FCSTD DOCUMENT  (FreeCAD 1.0R39319 (Git))
Label: KNOB-TEK2_assembly_tool_assy
License: All rights reserved
LicenseURL: https://en.wikipedia.org/wiki/All_rights_reserved
objects: App::DocumentObjectGroup×3, App::Link×3, PartDesign::CoordinateSystem×1, App::FeaturePython×1, App::Part×1
note: 1 computed .brp shape members not serialized (recipe doc carries the construction recipe); baked Part::Feature solids carry a one-line shape summary decoded from their .brp
EXTERNAL_REF file=../../Mechanical/Design/KNOB-TEK2/KNOB-TEK2.FCStd obj=LCS_1
EXTERNAL_REF file=../../Mechanical/Design/KNOB-TEK2/KNOB-TEK2.FCStd obj=Body
EXTERNAL_REF file=../../Mechanical/Design/KNOB-TEK2/KNOB-TEK2.FCStd obj=LCS_2
EXTERNAL_REF file=../../Mechanical/Design/PLASTIC-TEK2-KNOB-INTERFACE/PLASTIC-TEK2-KNOB-INTERFACE.FCStd obj=LCS_1
EXTERNAL_REF file=../../Mechanical/Design/PLASTIC-TEK2-KNOB-INTERFACE/PLASTIC-TEK2-KNOB-INTERFACE.FCStd obj=Body
EXTERNAL_REF file=KNOB-TEK2_assembly_tool.FCStd obj=LCS_1
EXTERNAL_REF file=../../Mechanical/Design/PLASTIC-TEK2-KNOB-INTERFACE/PLASTIC-TEK2-KNOB-INTERFACE.FCStd obj=LCS_3
EXTERNAL_REF file=KNOB-TEK2_assembly_tool.FCStd obj=Body

FEATURE [App::DocumentObjectGroup] Parts
FEATURE [PartDesign::CoordinateSystem] LCS_Origin
  AttacherType = Attacher::AttachEngine3D
  AttachmentSupport = -> [X_Axis]
  MapMode = 2
FEATURE [App::DocumentObjectGroup] Constraints
FEATURE [App::FeaturePython] Variables  # WARN: FeaturePython — macro-defined, semantics opaque (R4)
  Type = App::PropertyContainer
FEATURE [App::DocumentObjectGroup] Configurations
FEATURE [App::Link] KNOB_TEK2  label="KNOB-TEK2"
  AttachedBy = #LCS_1
  AttachedTo = Parent Assembly#LCS_Origin
  AttachmentOffset = pos=(0,0,0) rot=(1,0,0;3.14159rad)
  LinkPlacement = pos=(-0.740493,1.4e-15,14) rot=(0.707107,0.707107,0;3.14159rad)
  LinkedObject = -> <external ../../Mechanical/Design/KNOB-TEK2/KNOB-TEK2.FCStd>#Body
  Placement = pos=(-0.740493,1.4e-15,14) rot=(0.707107,0.707107,0;3.14159rad)
  SolverId = Asm4EE
  expr: Placement = LCS_Origin.Placement * AttachmentOffset * KNOB_TEK2#LCS_1.Placement ^ -1
FEATURE [App::Link] PLASTIC_TEK2_KNOB_INTERFACE  label="PLASTIC-TEK2-KNOB-INTERFACE"
  AttachedBy = #LCS_1
  AttachedTo = KNOB_TEK2#LCS_2
  AttachmentOffset = pos=(0,0,0) rot=(0.707107,0.707107,0;3.14159rad)
  LinkPlacement = pos=(-0.740493,-2e-16,4.75) rot=(0.708119,-0.706093,0;3.14159rad)
  LinkedObject = -> <external ../../Mechanical/Design/PLASTIC-TEK2-KNOB-INTERFACE/PLASTIC-TEK2-KNOB-INTERFACE.FCStd>#Body
  Placement = pos=(-0.740493,-2e-16,4.75) rot=(0.708119,-0.706093,0;3.14159rad)
  SolverId = Asm4EE
  expr: Placement = KNOB_TEK2.Placement * KNOB_TEK2#LCS_2.Placement * AttachmentOffset * PLASTIC_TEK2_KNOB_INTERFACE#LCS_1.Placement ^ -1
FEATURE [App::Link] Body
  AttachedBy = #LCS_1
  AttachedTo = PLASTIC_TEK2_KNOB_INTERFACE#LCS_3
  AttachmentOffset = pos=(0,0,0) rot=(0,-1,0;3.14159rad)
  LinkPlacement = pos=(-0.740493,4e-16,9.5) rot=(0,0,1;1.57366rad)
  LinkedObject = -> <external KNOB-TEK2_assembly_tool.FCStd>#Body
  Placement = pos=(-0.740493,4e-16,9.5) rot=(0,0,1;1.57366rad)
  SolverId = Asm4EE
  expr: Placement = PLASTIC_TEK2_KNOB_INTERFACE.Placement * PLASTIC_TEK2_KNOB_INTERFACE#LCS_3.Placement * AttachmentOffset * KNOB_TEK2_assembly_tool#LCS_1.Placement ^ -1
FEATURE [App::Part] Assembly
  AssemblyType = Part::Link
  Group = -> [LCS_Origin,Constraints,Variables,Configurations,KNOB_TEK2,PLASTIC_TEK2_KNOB_INTERFACE,Body]
  Origin = -> Origin
  Type = Assembly

RESOLVED EXTERNAL PARTS (link-assembly join: the EXTERNAL_REF files above that resolve inside this repo's crawl, each included once):
---- part ../../Mechanical/Design/KNOB-TEK2/KNOB-TEK2.FCStd = doc fcstd_0a6eb00ad0a5 ----
FCSTD DOCUMENT  (FreeCAD 1.0R39319 (Git))
Label: KNOB-TEK2
License: All rights reserved
LicenseURL: https://en.wikipedia.org/wiki/All_rights_reserved
objects: TechDraw::DrawViewDimension×14, Sketcher::SketchObject×7, TechDraw::DrawViewPart×5, TechDraw::DrawHatch×5, TechDraw::DrawViewBalloon×4, TechDraw::DrawViewAnnotation×2, PartDesign::Pocket×2, PartDesign::CoordinateSystem×2, Part::Feature×1, PartDesign::Plane×1, PartDesign::Pad×1, PartDesign::Boolean×1, TechDraw::DrawSVGTemplate×1, PartDesign::Fillet×1, PartDesign::Body×1, TechDraw::DrawComplexSection×1, TechDraw::DrawViewDimExtent×1, TechDraw::DrawPage×1
note: 58 computed .brp shape members not serialized (recipe doc carries the construction recipe); baked Part::Feature solids carry a one-line shape summary decoded from their .brp

FEATURE [Part::Feature] Part__Feature  label="alu_potmeter_002_04"
  shape: bbox 38.3 x 38.3 x 17.53 mm, 68 faces (baked)
FEATURE [PartDesign::Plane] DatumPlane
  AttachmentOffset = pos=(0,0,4.5) rot=(0,0,1;0rad)
  AttachmentSupport = -> [XY_Plane]
  Length = 60
  MapMode = 5
  Placement = pos=(0,0,4.5) rot=(0,0,1;0rad)
  ResizeMode = 0
  Width = 60
FEATURE [Sketcher::SketchObject] Sketch
  ArcFitTolerance = 0
  AttachmentSupport = -> [XY_Plane]
  FullyConstrained = true
  MakeInternals = false
  MapMode = 2
  sketch-geometry (1):
    g0: Circle CenterX=0 CenterY=0 CenterZ=0 NormalX=0 NormalY=0 NormalZ=1 AngleXU=0 Radius=15
  constraints (2):
    c: Coincident(g0,g-1)
    c: Diameter(g0) = 30
FEATURE [PartDesign::Pad] Pad
  Direction = (0,0,1)
  Length = 15
  Length2 = 10
  Profile = -> Sketch
  ReferenceAxis = -> Sketch [N_Axis]
  Refine = true
  Suppressed = false
  Type = 0
FEATURE [Sketcher::SketchObject] Sketch001
  ArcFitTolerance = 0
  AttachmentSupport = -> [DatumPlane]
  FullyConstrained = true
  MakeInternals = false
  MapMode = 5
  Placement = pos=(0,0,4.5) rot=(0,0,1;0rad)
  sketch-geometry (7):
    g0: ArcOfCircle CenterX=0 CenterY=0 CenterZ=0 NormalX=0 NormalY=0 NormalZ=1 AngleXU=0 Radius=7 StartAngle=5.63968 EndAngle=10.0683
    g1: LineSegment StartX=-4 StartY=-5 StartZ=0 EndX=4 EndY=-5 EndZ=0
    g2: Circle [constr] CenterX=0 CenterY=0 CenterZ=0 NormalX=0 NormalY=0 NormalZ=1 AngleXU=0 Radius=4.25
    g3: LineSegment [constr] StartX=0 StartY=-4.25 StartZ=0 EndX=0 EndY=-5 EndZ=0
    g4: ArcOfCircle CenterX=-4 CenterY=-3 CenterZ=0 NormalX=0 NormalY=0 NormalZ=1 AngleXU=0 Radius=2 StartAngle=3.78509 EndAngle=4.71239
    g5: ArcOfCircle CenterX=4 CenterY=-3 CenterZ=0 NormalX=0 NormalY=0 NormalZ=1 AngleXU=0 Radius=2 StartAngle=4.71239 EndAngle=5.63968
    g6: GeomPoint [constr] X=0 Y=7 Z=0
  constraints (20):
    c: Coincident(g0,g-1)
    c: Diameter(g0) = 14
    c: Horizontal(g1)
    c: Coincident(g2,g0)
    c: Diameter(g2) = 8.5
    c: PointOnObject(g3,g2)
    c: PointOnObject(g3,g1)
    c: Vertical(g3)
    c: PointOnObject(g3,g-2)
    c: DistanceY(g3,g3) = 0.75
    c: Tangent(g1,g4) = -1.5708
    c: Tangent(g0,g4) = -1.5708
    c: Tangent(g1,g5) = -1.5708
    c: Tangent(g0,g5) = -1.5708
    c: Equal(g5,g4)
    c: Diameter(g5) = 4
    c: DistanceY(g3,g0) = 5
    c: PointOnObject(g6,g0)
    c: PointOnObject(g6,g-2)
    c: DistanceY(g3,g6) = 12
FEATURE [PartDesign::Boolean] Boolean
  BaseFeature = -> Pad
  Group = -> [Part__Feature]
  Refine = true
  Suppressed = false
  Type = 0
  UsePlacement = false
FEATURE [TechDraw::DrawSVGTemplate] Template
  EditableTexts = COLOR=Sandblasted, black anodized (RAL code: 9004); CreationDate=2024/08/27; E.G.APPROVED=APPROVED; FC-Scale=2:1; FC-Title=KNOB-TEK2; IntechStudioLtd.=Intech Studio Ltd.; MATERIAL=Aluminum 6061-T6; REV=03; STANDARD=DIN 16742-TG5
  Height = 297
  Orientation = 1
  Template = <userpath>/Documents/grid-hardware/Manufacturing/FreeCAD_technical_drawing_template/A3_LandscapeTD_MODIFIED.svg
  Width = 420
FEATURE [Sketcher::SketchObject] Sketch002
  ArcFitTolerance = 0
  AttachmentSupport = -> [YZ_Plane]
  FullyConstrained = true
  MakeInternals = false
  MapMode = 5
  Placement = pos=(0,0,0) rot=(0.57735,0.57735,0.57735;2.0944rad)
  sketch-geometry (1):
    g0: LineSegment StartX=0 StartY=20 StartZ=0 EndX=0 EndY=-5 EndZ=0
  constraints (4):
    c: PointOnObject(g0,g-2)
    c: PointOnObject(g0,g-2)
    c: DistanceY(g0,g0) = 25
    c: DistanceY(g0,g-1) = 5
FEATURE [TechDraw::DrawViewAnnotation] Annotation
  Font = osifont
  LineSpace = 100
  LockPosition = false
  MaxWidth = -1
  Rotation = 0
  Scale = 2
  ScaleType = 0
  Text = Non-aesthetical side (purple): | No burrs
  TextSize = 5
  TextStyle = 0
  X = 278.355
  Y = 88.8334
FEATURE [Sketcher::SketchObject] Sketch004
  ArcFitTolerance = 0
  AttachmentSupport = -> [XY_Plane]
  FullyConstrained = true
  MakeInternals = false
  MapMode = 5
  sketch-geometry (1):
    g0: Circle CenterX=0 CenterY=0 CenterZ=0 NormalX=0 NormalY=0 NormalZ=1 AngleXU=0 Radius=10
  constraints (2):
    c: Coincident(g0,g-1)
    c: Diameter(g0) = 20
FEATURE [PartDesign::Pocket] Pocket001
  BaseFeature = -> Boolean
  Direction = (0,0,-1)
  Length = 4.5
  Length2 = 5
  Profile = -> Sketch004
  ReferenceAxis = -> Sketch004 [N_Axis]
  Refine = true
  Reversed = true
  Suppressed = false
  Type = 0
FEATURE [PartDesign::Pocket] Pocket
  BaseFeature = -> Pocket001
  Direction = (0,0,-1)
  Length = 9.5
  Length2 = 5
  Profile = -> Sketch001
  ReferenceAxis = -> Sketch001 [N_Axis]
  Refine = true
  Reversed = true
  Suppressed = false
  Type = 0
FEATURE [TechDraw::DrawViewAnnotation] Annotation001
  Font = osifont
  LineSpace = 100
  LockPosition = false
  MaxWidth = -1
  Rotation = 0
  Scale = 2
  ScaleType = 0
  Text = Section A-A
  TextSize = 4
  TextStyle = 0
  X = 199.631
  Y = 206.549
FEATURE [Sketcher::SketchObject] Sketch005
  ArcFitTolerance = 0
  AttachmentSupport = -> [DatumPlane]
  FullyConstrained = true
  MakeInternals = false
  MapMode = 5
  Placement = pos=(0,0,4.5) rot=(0,0,1;0rad)
  sketch-geometry (1):
    g0: Circle CenterX=0 CenterY=0 CenterZ=0 NormalX=0 NormalY=0 NormalZ=1 AngleXU=0 Radius=3.5
  constraints (2):
    c: Coincident(g0,g-1)
    c: Diameter(g0) = 7
FEATURE [PartDesign::Fillet] Fillet
  Base = -> Pocket [Edge136]
  BaseFeature = -> Pocket
  Radius = 1
  SupportTransform = false
  Suppressed = false
  UseAllEdges = false
FEATURE [Sketcher::SketchObject] Sketch006
  ArcFitTolerance = 0
  AttachmentSupport = -> [XY_Plane]
  FullyConstrained = true
  MakeInternals = false
  MapMode = 5
  sketch-geometry (5):
    g0: Circle CenterX=0 CenterY=0 CenterZ=0 NormalX=0 NormalY=0 NormalZ=1 AngleXU=0 Radius=6.975
    g1: Circle CenterX=0 CenterY=0 CenterZ=0 NormalX=0 NormalY=0 NormalZ=1 AngleXU=0 Radius=4.3
    g2: LineSegment StartX=-4.88876 StartY=4.975 StartZ=0 EndX=4.88876 EndY=4.975 EndZ=0
    g3: GeomPoint [constr] X=0 Y=-6.975 Z=0
    g4: GeomPoint [constr] X=0 Y=4.3 Z=0
  constraints (13):
    c: Coincident(g0,g-1)
    c: Coincident(g1,g0)
    c: PointOnObject(g2,g0)
    c: PointOnObject(g2,g0)
    c: Horizontal(g2)
    c: Diameter(g0) = 13.95
    c: Diameter(g1) = 8.6
    c: PointOnObject(g3,g0)
    c: PointOnObject(g3,g-2)
    c: DistanceY(g3,g2) = 11.95
    c: PointOnObject(g4,g1)
    c: DistanceY(g4,g2) = 0.675
    c: PointOnObject(g4,g-2)
FEATURE [Sketcher::SketchObject] Sketch007
  ArcFitTolerance = 0
  AttachmentSupport = -> [XY_Plane]
  FullyConstrained = true
  MakeInternals = false
  MapMode = 5
  sketch-geometry (4):
    g0: Circle CenterX=0 CenterY=0 CenterZ=0 NormalX=0 NormalY=0 NormalZ=1 AngleXU=0 Radius=0.1
    g1: Circle CenterX=0 CenterY=0.1 CenterZ=0 NormalX=0 NormalY=0 NormalZ=1 AngleXU=0 Radius=3.475
    g2: Circle CenterX=0 CenterY=-0.1 CenterZ=0 NormalX=0 NormalY=0 NormalZ=1 AngleXU=0 Radius=2.95
    g3: LineSegment StartX=0 StartY=-3.05 StartZ=0 EndX=0 EndY=-3.375 EndZ=0
  constraints (13):
    c: Coincident(g0,g-1)
    c: Diameter(g0) = 0.2
    c: PointOnObject(g1,g-2)
    c: PointOnObject(g1,g0)
    c: Diameter(g1) = 6.95
    c: PointOnObject(g2,g0)
    c: PointOnObject(g2,g-2)
    c: Diameter(g2) = 5.9
    c: PointOnObject(g3,g2)
    c: PointOnObject(g3,g1)
    c: Vertical(g3)
    c: PointOnObject(g3,g-2)
    c: DistanceY(g3,g3) = 0.325
FEATURE [PartDesign::CoordinateSystem] LCS_1
  AttacherType = Attacher::AttachEngine3D
  AttachmentSupport = -> [Fillet]
  MapMode = 45
  Placement = pos=(5e-16,0.740493,14) rot=(0,0,1;1.5708rad)
FEATURE [PartDesign::CoordinateSystem] LCS_2
  AttacherType = Attacher::AttachEngine3D
  AttachmentSupport = -> [Fillet]
  MapMode = 5
  Placement = pos=(0,0,14) rot=(1,0,0;3.14159rad)
FEATURE [PartDesign::Body] Body  label="KNOB-TEK2"
  AllowCompound = false
  Group = -> [DatumPlane,Sketch,Pad,Boolean,Pocket001,Sketch001,Pocket,Sketch002,Sketch004,Sketch005,Fillet,Sketch006,Sketch007,LCS_1,LCS_2]
  Origin = -> Origin
  Tip = -> Fillet
FEATURE [TechDraw::DrawViewPart] View
  CoarseView = false
  Direction = (-1,0,-3e-06)
  Focus = 100
  HardHidden = false
  IsoCount = 0
  IsoHidden = false
  IsoVisible = true
  LockPosition = false
  Perspective = false
  Rotation = 0
  Scale = 2
  ScaleType = 2
  ScrubCount = 0
  SeamHidden = false
  SeamVisible = true
  SmoothHidden = false
  SmoothVisible = true
  Source = -> [Body]
  X = 71.6241
  XDirection = (0,-1,0)
  Y = 240.603
FEATURE [TechDraw::DrawComplexSection] ComplexSection  label="Section A - A"
  BaseView = -> View
  CoarseView = false
  CutSurfaceDisplay = 3
  CuttingToolWireObject = -> Sketch002
  Direction = (0,1,-1e-16)
  FileGeomPattern = C:/Program Files/FreeCAD 0.21/data/Mod/TechDraw/PAT/FCPAT.pat
  FileHatchPattern = C:/Program Files/FreeCAD 0.21/data/Mod/TechDraw/Patterns/simple.svg
  Focus = 100
  FuseBeforeCut = false
  HardHidden = false
  HatchOffset = (0,0,0)
  HatchRotation = 0
  HatchScale = 1
  IsoCount = 0
  IsoHidden = false
  IsoVisible = true
  LockPosition = false
  NameGeomPattern = Gyémánt bevonatú
  Perspective = false
  ProjectionStrategy = 0
  Rotation = -90
  Scale = 2
  ScaleType = 0
  ScrubCount = 0
  SeamHidden = false
  SeamVisible = true
  SectionDirection = 4
  SectionLineStretch = 1
  SectionNormal = (0,1,-1e-16)
  SectionOrigin = (0,0,0)
  SectionSymbol = A
  SmoothHidden = false
  SmoothVisible = true
  Source = -> [Body]
  TrimAfterCut = false
  UsePreviousCut = false
  X = 199.631
  XDirection = (3e-06,-1e-16,-1)
  Y = 238.539
FEATURE [TechDraw::DrawViewPart] View001
  CoarseView = false
  Direction = (-3e-06,0,1)
  Focus = 100
  HardHidden = false
  IsoCount = 0
  IsoHidden = false
  IsoVisible = true
  LockPosition = false
  Perspective = false
  Rotation = 0
  Scale = 2
  ScaleType = 0
  ScrubCount = 0
  SeamHidden = false
  SeamVisible = true
  SmoothHidden = false
  SmoothVisible = true
  Source = -> [Body]
  X = 71.7073
  XDirection = (1,0,3e-06)
  Y = 150.924
FEATURE [TechDraw::DrawViewDimension] Dimension010
  AngleOverride = false
  Arbitrary = false
  ArbitraryTolerances = false
  EqualTolerance = true
  ExtensionAngle = 0
  FormatSpec = %.2w
  FormatSpecOverTolerance = %+.2w
  FormatSpecUnderTolerance = %+.2w
  Inverted = false
  LineAngle = 0
  LockPosition = false
  MeasureType = 1
  OverTolerance = 0
  References2D = -> [ComplexSection]
  Rotation = 0
  Scale = 2
  ScaleType = 0
  TheoreticalExact = false
  Type = 2
  UnderTolerance = 0
  X = 46.1971
  Y = -10.7931
FEATURE [TechDraw::DrawViewDimension] Dimension014
  AngleOverride = false
  Arbitrary = false
  ArbitraryTolerances = true
  EqualTolerance = false
  ExtensionAngle = 0
  FormatSpec = %.2w
  FormatSpecOverTolerance = +0
  FormatSpecUnderTolerance = -0.1
  Inverted = false
  LineAngle = 0
  LockPosition = false
  MeasureType = 1
  OverTolerance = 0
  References2D = -> [ComplexSection]
  Rotation = 0
  Scale = 2
  ScaleType = 0
  TheoreticalExact = false
  Type = 2
  UnderTolerance = 0
  X = 56.4159
  Y = 6.5209
FEATURE [TechDraw::DrawViewDimension] Dimension016
  AngleOverride = false
  Arbitrary = false
  ArbitraryTolerances = false
  EqualTolerance = true
  ExtensionAngle = 0
  FormatSpec = 12× %.2w
  FormatSpecOverTolerance = %+.2w
  FormatSpecUnderTolerance = %+.2w
  Inverted = false
  LineAngle = 0
  LockPosition = false
  MeasureType = 1
  OverTolerance = 0
  References2D = -> [View001]
  Rotation = 0
  Scale = 2
  ScaleType = 0
  TheoreticalExact = false
  Type = 2
  UnderTolerance = 0
  X = -56.7628
  Y = 0.276868
FEATURE [TechDraw::DrawViewPart] View002
  CoarseView = false
  Direction = (3e-06,1e-06,-1)
  Focus = 100
  HardHidden = false
  IsoCount = 0
  IsoHidden = false
  IsoVisible = true
  LockPosition = false
  Perspective = false
  Rotation = 0
  Scale = 2
  ScaleType = 0
  ScrubCount = 0
  SeamHidden = false
  SeamVisible = true
  SmoothHidden = false
  SmoothVisible = true
  Source = -> [Body]
  X = 200.492
  XDirection = (1,-3e-12,3e-06)
  Y = 152.25
FEATURE [TechDraw::DrawViewPart] View003
  CoarseView = false
  Direction = (-0.57735,0.57735,-0.57735)
  Focus = 100
  HardHidden = false
  IsoCount = 0
  IsoHidden = false
  IsoVisible = true
  LockPosition = false
  Perspective = false
  Rotation = 0
  Scale = 2
  ScaleType = 2
  ScrubCount = 0
  SeamHidden = false
  SeamVisible = true
  SmoothHidden = false
  SmoothVisible = true
  Source = -> [Body]
  X = 358.57
  XDirection = (-0.707102,-0.707111,-9.2376e-06)
  Y = 140.843
FEATURE [TechDraw::DrawViewPart] View004
  CoarseView = false
  Direction = (-0.57735,0.57735,0.57735)
  Focus = 100
  HardHidden = false
  IsoCount = 0
  IsoHidden = false
  IsoVisible = true
  LockPosition = false
  Perspective = false
  Rotation = 0
  Scale = 2
  ScaleType = 2
  ScrubCount = 0
  SeamHidden = false
  SeamVisible = true
  SmoothHidden = false
  SmoothVisible = true
  Source = -> [Body]
  X = 357.533
  XDirection = (-0.707111,-0.707101,-9.2376e-06)
  Y = 230.245
FEATURE [TechDraw::DrawHatch] Hatch  label="HatchF1"
  HatchPattern = C:/Program Files/FreeCAD 0.21/data/Mod/TechDraw/Patterns/solid.svg
  Source = -> View003 [Face1,Face44,Face15,Face7,Face3,Face19]
FEATURE [TechDraw::DrawHatch] Hatch001  label="Hatch001F13"
  HatchPattern = C:/Program Files/FreeCAD 0.21/data/Mod/TechDraw/Patterns/solid.svg
  Source = -> View004 [Face13,Face4,Face5,Face1,Face3,Face18,Face17,Face14,Face12,Face9,Face8,Face6,Face7,Face10,Face19,Face16,Face15,Face11,Face27,Face26,Face23,Face22,Face20,Face21,Face24,Face28,Face25]
FEATURE [TechDraw::DrawHatch] Hatch002  label="Hatch002F24"
  HatchPattern = C:/Program Files/FreeCAD 0.21/data/Mod/TechDraw/Patterns/solid.svg
  Source = -> View003 [Face24,Face25,Face28,Face29,Face32,Face33,Face36,Face37,Face38,Face35,Face34,Face31,Face30,Face27,Face26,Face23,Face22,Face20,Face21,Face11,Face8,Face6,Face4,Face5,Face9,Face10,Face13,Face17]
FEATURE [TechDraw::DrawViewBalloon] Balloon003
  BubbleShape = 1
  EndType = 3
  EndTypeScale = 1
  KinkLength = 0
  LockPosition = false
  OriginX = -14.9594
  OriginY = -6.7795
  Rotation = 0
  Scale = 2
  ScaleType = 0
  ShapeScale = 1
  SourceView = -> View003
  TextWrapLen = -1
  X = -29.1537
  Y = -19.8858
FEATURE [TechDraw::DrawViewDimension] Dimension027
  AngleOverride = false
  Arbitrary = false
  ArbitraryTolerances = false
  EqualTolerance = true
  ExtensionAngle = 0
  FormatSpec = ⌀%.2w
  FormatSpecOverTolerance = %+.2w
  FormatSpecUnderTolerance = %+.2w
  Inverted = false
  LineAngle = 0
  LockPosition = false
  MeasureType = 1
  OverTolerance = 0
  References2D = -> [View002]
  Rotation = 0
  Scale = 2
  ScaleType = 0
  TheoreticalExact = false
  Type = 5
  UnderTolerance = 0
  X = 58.2687
  Y = -4.50785
FEATURE [TechDraw::DrawViewDimExtent] DimExtent
  AngleOverride = false
  Arbitrary = false
  ArbitraryTolerances = false
  DirExtent = 0
  EqualTolerance = true
  ExtensionAngle = 0
  FormatSpec = ⌀%.2w
  FormatSpecOverTolerance = %+.2w
  FormatSpecUnderTolerance = %+.2w
  Inverted = false
  LineAngle = 0
  LockPosition = false
  MeasureType = 1
  OverTolerance = 0
  References2D = -> [View001]
  Rotation = 0
  Scale = 2
  ScaleType = 0
  Source = -> [View001]
  TheoreticalExact = false
  Type = 1
  UnderTolerance = 0
  X = -0.58901
  Y = -46.3131
FEATURE [TechDraw::DrawViewBalloon] Balloon
  BubbleShape = 6
  EndType = 6
  EndTypeScale = 1
  KinkLength = -0.1
  LockPosition = false
  OriginX = 19.3129
  OriginY = -26.049
  Rotation = 0
  Scale = 2
  ScaleType = 0
  ShapeScale = 1
  SourceView = -> DimExtent
  Text = A
  TextWrapLen = -1
  X = 24.4472
  Y = -26.0434
FEATURE [TechDraw::DrawViewDimension] Dimension029
  AngleOverride = false
  Arbitrary = false
  ArbitraryTolerances = false
  EqualTolerance = true
  ExtensionAngle = 0
  FormatSpec = ⌀%.2w
  FormatSpecOverTolerance = %+.2w
  FormatSpecUnderTolerance = %+.2w
  Inverted = false
  LineAngle = 0
  LockPosition = false
  MeasureType = 1
  OverTolerance = 0.05
  References2D = -> [ComplexSection]
  Rotation = 0
  Scale = 2
  ScaleType = 0
  TheoreticalExact = false
  Type = 1
  UnderTolerance = -0.05
  X = -51.7957
  Y = -20.9962
FEATURE [TechDraw::DrawViewBalloon] Balloon004
  BubbleShape = 6
  EndType = 6
  EndTypeScale = 1
  KinkLength = 0
  LockPosition = false
  OriginX = -30.2962
  OriginY = -14.1405
  Rotation = 0
  Scale = 2
  ScaleType = 0
  ShapeScale = 1
  SourceView = -> Dimension029
  Text = ◎|⌀ 0.2|A
  TextWrapLen = -1
  X = -22.8396
  Y = -16.0535
FEATURE [TechDraw::DrawViewDimension] Dimension030
  AngleOverride = false
  Arbitrary = false
  ArbitraryTolerances = false
  EqualTolerance = true
  ExtensionAngle = 0
  FormatSpec = R%.2w
  FormatSpecOverTolerance = %+.2w
  FormatSpecUnderTolerance = %+.2w
  Inverted = false
  LineAngle = 0
  LockPosition = false
  MeasureType = 1
  OverTolerance = 0
  References2D = -> [View002]
  Rotation = 0
  Scale = 2
  ScaleType = 0
  TheoreticalExact = false
  Type = 4
  UnderTolerance = 0
  X = 54.5926
  Y = 26.3888
FEATURE [TechDraw::DrawHatch] Hatch003  label="Hatch003F14"
  HatchPattern = C:/Program Files/FreeCAD 0.21/data/Mod/TechDraw/Patterns/solid.svg
  Source = -> View003 [Face14,Face16]
FEATURE [TechDraw::DrawHatch] Hatch004  label="Hatch004F18"
  HatchPattern = C:/Program Files/FreeCAD 0.21/data/Mod/TechDraw/Patterns/solid.svg
  Source = -> View003 [Face18,Face12]
FEATURE [TechDraw::DrawViewDimension] Dimension033
  AngleOverride = false
  Arbitrary = false
  ArbitraryTolerances = false
  EqualTolerance = true
  ExtensionAngle = 0
  FormatSpec = 12× %.2w
  FormatSpecOverTolerance = %+.2w
  FormatSpecUnderTolerance = %+.2w
  Inverted = false
  LineAngle = 0
  LockPosition = false
  MeasureType = 1
  OverTolerance = 0
  References2D = -> [View001]
  Rotation = 0
  Scale = 2
  ScaleType = 0
  TheoreticalExact = false
  Type = 2
  UnderTolerance = 0
  X = -46.3715
  Y = 0.067851
FEATURE [TechDraw::DrawViewDimension] Dimension038
  AngleOverride = false
  Arbitrary = false
  ArbitraryTolerances = false
  EqualTolerance = true
  ExtensionAngle = 0
  FormatSpec = %.2w
  FormatSpecOverTolerance = %+.2w
  FormatSpecUnderTolerance = %+.2w
  Inverted = false
  LineAngle = 0
  LockPosition = false
  MeasureType = 1
  OverTolerance = 0.05
  References2D = -> [View002]
  Rotation = 0
  Scale = 2
  ScaleType = 0
  TheoreticalExact = false
  Type = 2
  UnderTolerance = -0.05
  X = -63.5296
  Y = 1.33773
FEATURE [TechDraw::DrawViewDimension] Dimension039
  AngleOverride = false
  Arbitrary = false
  ArbitraryTolerances = false
  EqualTolerance = true
  ExtensionAngle = 0
  FormatSpec = R%.2w
  FormatSpecOverTolerance = %+.2w
  FormatSpecUnderTolerance = %+.2w
  Inverted = false
  LineAngle = 0
  LockPosition = false
  MeasureType = 1
  OverTolerance = 0
  References2D = -> [ComplexSection]
  Rotation = 0
  Scale = 2
  ScaleType = 0
  TheoreticalExact = false
  Type = 4
  UnderTolerance = 0
  X = -24.8071
  Y = 25.4275
FEATURE [TechDraw::DrawViewDimension] Dimension
  AngleOverride = false
  Arbitrary = false
  ArbitraryTolerances = false
  EqualTolerance = true
  ExtensionAngle = 0
  FormatSpec = R%.2w
  FormatSpecOverTolerance = %+.2w
  FormatSpecUnderTolerance = %+.2w
  Inverted = false
  LineAngle = 0
  LockPosition = false
  MeasureType = 1
  OverTolerance = 0
  References2D = -> [ComplexSection]
  Rotation = 0
  Scale = 2
  ScaleType = 0
  TheoreticalExact = false
  Type = 4
  UnderTolerance = 0
  X = -22.3763
  Y = 37.775
FEATURE [TechDraw::DrawViewDimension] Dimension040
  AngleOverride = false
  Arbitrary = false
  ArbitraryTolerances = false
  EqualTolerance = true
  ExtensionAngle = 0
  FormatSpec = %.2w
  FormatSpecOverTolerance = %+.2w
  FormatSpecUnderTolerance = %+.2w
  Inverted = false
  LineAngle = 0
  LockPosition = false
  MeasureType = 1
  OverTolerance = 0
  References2D = -> [ComplexSection]
  Rotation = 0
  Scale = 2
  ScaleType = 0
  TheoreticalExact = false
  Type = 2
  UnderTolerance = 0
  X = 50.8041
  Y = -1.3095
FEATURE [TechDraw::DrawViewDimension] Dimension041
  AngleOverride = false
  Arbitrary = false
  ArbitraryTolerances = false
  EqualTolerance = true
  ExtensionAngle = 0
  FormatSpec = %.2w
  FormatSpecOverTolerance = %+.2w
  FormatSpecUnderTolerance = %+.2w
  Inverted = false
  LineAngle = 0
  LockPosition = false
  MeasureType = 1
  OverTolerance = 0
  References2D = -> [View]
  Rotation = 0
  Scale = 2
  ScaleType = 0
  TheoreticalExact = false
  Type = 2
  UnderTolerance = 0
  X = 49.3362
  Y = 2.45968
FEATURE [TechDraw::DrawViewDimension] Dimension042
  AngleOverride = false
  Arbitrary = false
  ArbitraryTolerances = false
  EqualTolerance = true
  ExtensionAngle = 0
  FormatSpec = 12× %.2w
  FormatSpecOverTolerance = %+.2w
  FormatSpecUnderTolerance = %+.2w
  Inverted = false
  LineAngle = 0
  LockPosition = false
  MeasureType = 1
  OverTolerance = 0
  References2D = -> [View001]
  Rotation = 0
  Scale = 2
  ScaleType = 0
  TheoreticalExact = false
  Type = 2
  UnderTolerance = 0
  X = -47.1912
  Y = 0.484682
FEATURE [TechDraw::DrawViewDimension] Dimension043
  AngleOverride = false
  Arbitrary = false
  ArbitraryTolerances = false
  EqualTolerance = true
  ExtensionAngle = 0
  FormatSpec = %.2w
  FormatSpecOverTolerance = %+.2w
  FormatSpecUnderTolerance = %+.2w
  Inverted = false
  LineAngle = 0
  LockPosition = false
  MeasureType = 1
  OverTolerance = 0
  References2D = -> [View002]
  Rotation = 0
  Scale = 2
  ScaleType = 0
  TheoreticalExact = false
  Type = 2
  UnderTolerance = 0
  X = -53.6468
  Y = 6.7345
FEATURE [TechDraw::DrawViewBalloon] Balloon005
  BubbleShape = 2
  EndType = 0
  EndTypeScale = 1
  KinkLength = 5
  LockPosition = false
  OriginX = 14.2219
  OriginY = 15.3271
  Rotation = 0
  Scale = 2
  ScaleType = 0
  ShapeScale = 1
  SourceView = -> ComplexSection
  Text = 3
  TextWrapLen = -1
  X = 8.32091
  Y = 13.2809
FEATURE [TechDraw::DrawPage] Page  label="KNOB-TEK2_Drawing"
  KeepUpdated = true
  NextBalloonIndex = 10
  ProjectionType = 0
  Scale = 2
  Template = -> Template
  Views = -> [View,ComplexSection,View001,View002,Dimension010,Dimension014,Annotation,Dimension016,View003,View004,Annotation001,Balloon003,Dimension027,DimExtent,Balloon,Dimension029,Balloon004,Dimension030,Dimension033,Dimension038,Dimension039,Dimension,Dimension040,Dimension041,Dimension042,Dimension043,Balloon005]
---- part ../../Mechanical/Design/PLASTIC-TEK2-KNOB-INTERFACE/PLASTIC-TEK2-KNOB-INTERFACE.FCStd = doc fcstd_a0d65299c5b8 ----
FCSTD DOCUMENT  (FreeCAD 1.0R39319 (Git))
Label: PLASTIC-TEK2-KNOB-INTERFACE
License: All rights reserved
LicenseURL: https://en.wikipedia.org/wiki/All_rights_reserved
objects: Sketcher::SketchObject×10, PartDesign::Pad×9, PartDesign::Plane×5, PartDesign::Chamfer×3, PartDesign::Body×3, PartDesign::CoordinateSystem×3, PartDesign::Boolean×2, PartDesign::Pocket×1
note: 74 computed .brp shape members not serialized (recipe doc carries the construction recipe); baked Part::Feature solids carry a one-line shape summary decoded from their .brp

FEATURE [Sketcher::SketchObject] Sketch
  ArcFitTolerance = 0
  AttachmentSupport = -> [XY_Plane]
  FullyConstrained = true
  MakeInternals = false
  MapMode = 5
  sketch-geometry (5):
    g0: LineSegment StartX=-2.81957 StartY=1.9 StartZ=0 EndX=2.81957 EndY=1.9 EndZ=0
    g1: ArcOfCircle CenterX=0 CenterY=0 CenterZ=0 NormalX=0 NormalY=0 NormalZ=1 AngleXU=0 Radius=3.4 StartAngle=2.54863 EndAngle=6.87615
    g2: LineSegment StartX=-4.71169 StartY=4.55 StartZ=0 EndX=4.71169 EndY=4.55 EndZ=0
    g3: GeomPoint [constr] X=1e-16 Y=4.55 Z=0
    g4: ArcOfCircle CenterX=0 CenterY=0 CenterZ=0 NormalX=0 NormalY=0 NormalZ=1 AngleXU=0 Radius=6.55 StartAngle=2.37365 EndAngle=7.05113
  constraints (13):
    c: Diameter(g1) = 6.8
    c: Coincident(g0,g1)
    c: Coincident(g0,g1)
    c: Horizontal(g0)
    c: Horizontal(g2)
    c: Symmetric(g2,g2,g3)
    c: Diameter(g4) = 13.1
    c: Coincident(g4,g2)
    c: Coincident(g4,g2)
    c: Coincident(g4,g1)
    c: DistanceY(g1,g2) = 4.55
    c: Coincident(g1,g-1)
    c: DistanceY(g1,g0) = 1.9
FEATURE [PartDesign::Pad] Pad
  Direction = (0,0,1)
  Length = 9.5
  Length2 = 10
  Midplane = true
  Profile = -> Sketch
  ReferenceAxis = -> Sketch [N_Axis]
  Suppressed = false
  Type = 0
FEATURE [Sketcher::SketchObject] Sketch002
  ArcFitTolerance = 0
  AttachmentSupport = -> [XY_Plane]
  FullyConstrained = true
  MakeInternals = false
  MapMode = 5
  sketch-geometry (41):
    g0: ArcOfCircle [constr] CenterX=0 CenterY=0 CenterZ=0 NormalX=0 NormalY=0 NormalZ=1 AngleXU=0 Radius=6.6 StartAngle=2.37043 EndAngle=7.05435
    g1: Circle CenterX=-5.65685 CenterY=3.4 CenterZ=0 NormalX=0 NormalY=0 NormalZ=1 AngleXU=0 Radius=0.5
    g2: LineSegment [constr] StartX=-4.73286 StartY=4.6 StartZ=0 EndX=4.73286 EndY=4.6 EndZ=0
    g3: Circle CenterX=-6.48224 CenterY=1.2412 CenterZ=0 NormalX=0 NormalY=0 NormalZ=1 AngleXU=0 Radius=0.5
    g4: Circle CenterX=-6.51272 CenterY=-1.0698 CenterZ=0 NormalX=0 NormalY=0 NormalZ=1 AngleXU=0 Radius=0.5
    g5: Circle CenterX=-4.27196 CenterY=-5.03094 CenterZ=0 NormalX=0 NormalY=0 NormalZ=1 AngleXU=0 Radius=0.5
    g6: Circle CenterX=-2.2755 CenterY=-6.19533 CenterZ=0 NormalX=0 NormalY=0 NormalZ=1 AngleXU=0 Radius=0.5
    g7: Circle CenterX=-4e-16 CenterY=-6.6 CenterZ=0 NormalX=0 NormalY=0 NormalZ=1 AngleXU=0 Radius=0.5
    g8: Circle CenterX=5.65685 CenterY=3.4 CenterZ=0 NormalX=0 NormalY=0 NormalZ=1 AngleXU=0 Radius=0.5
    g9: Circle CenterX=-5.74456 CenterY=-3.24962 CenterZ=0 NormalX=0 NormalY=0 NormalZ=1 AngleXU=0 Radius=0.5
    g10: Circle CenterX=6.48224 CenterY=1.2412 CenterZ=0 NormalX=0 NormalY=0 NormalZ=1 AngleXU=0 Radius=0.5
    g11: Circle CenterX=4.27196 CenterY=-5.03094 CenterZ=0 NormalX=0 NormalY=0 NormalZ=1 AngleXU=0 Radius=0.5
    g12: Circle CenterX=5.74456 CenterY=-3.24962 CenterZ=0 NormalX=0 NormalY=0 NormalZ=1 AngleXU=0 Radius=0.5
    g13: Circle CenterX=2.2755 CenterY=-6.19533 CenterZ=0 NormalX=0 NormalY=0 NormalZ=1 AngleXU=0 Radius=0.5
    g14: Circle CenterX=6.51272 CenterY=-1.0698 CenterZ=0 NormalX=0 NormalY=0 NormalZ=1 AngleXU=0 Radius=0.5
    g15: LineSegment [constr] StartX=-5.65685 StartY=3.4 StartZ=0 EndX=-6.48224 EndY=1.2412 EndZ=0
    g16: LineSegment [constr] StartX=-6.48224 StartY=1.2412 StartZ=0 EndX=-6.51272 EndY=-1.0698 EndZ=0
    g17: LineSegment [constr] StartX=-6.51272 StartY=-1.0698 StartZ=0 EndX=-5.74456 EndY=-3.24962 EndZ=0
    g18: LineSegment [constr] StartX=-5.74456 StartY=-3.24962 StartZ=0 EndX=-4.27196 EndY=-5.03094 EndZ=0
    g19: LineSegment [constr] StartX=-4.27196 StartY=-5.03094 StartZ=0 EndX=-2.2755 EndY=-6.19533 EndZ=0
    g20: LineSegment [constr] StartX=-2.2755 StartY=-6.19533 StartZ=0 EndX=-4e-16 EndY=-6.6 EndZ=0
    g21: LineSegment [constr] StartX=-4e-16 StartY=-6.6 StartZ=0 EndX=2.2755 EndY=-6.19533 EndZ=0
    g22: LineSegment [constr] StartX=2.2755 StartY=-6.19533 StartZ=0 EndX=4.27196 EndY=-5.03094 EndZ=0
    g23: LineSegment [constr] StartX=4.27196 StartY=-5.03094 StartZ=0 EndX=5.74456 EndY=-3.24962 EndZ=0
    g24: LineSegment [constr] StartX=5.74456 StartY=-3.24962 StartZ=0 EndX=6.51272 EndY=-1.0698 EndZ=0
    g25: LineSegment [constr] StartX=6.51272 StartY=-1.0698 StartZ=0 EndX=6.48224 EndY=1.2412 EndZ=0
    g26: LineSegment [constr] StartX=6.48224 StartY=1.2412 StartZ=0 EndX=5.65685 EndY=3.4 EndZ=0
    g27: Circle CenterX=-3.45 CenterY=4.6 CenterZ=0 NormalX=0 NormalY=0 NormalZ=1 AngleXU=0 Radius=0.5
    g28: Circle CenterX=-1.15 CenterY=4.6 CenterZ=0 NormalX=0 NormalY=0 NormalZ=1 AngleXU=0 Radius=0.5
    g29: LineSegment [constr] StartX=-3.45 StartY=4.6 StartZ=0 EndX=-1.15 EndY=4.6 EndZ=0
    g30: Circle CenterX=1.15 CenterY=4.6 CenterZ=0 NormalX=0 NormalY=0 NormalZ=1 AngleXU=0 Radius=0.5
    g31: LineSegment [constr] StartX=-1.15 StartY=4.6 StartZ=0 EndX=1.15 EndY=4.6 EndZ=0
    g32: Circle CenterX=3.45 CenterY=4.6 CenterZ=0 NormalX=0 NormalY=0 NormalZ=1 AngleXU=0 Radius=0.5
    g33: LineSegment [constr] StartX=1.15 StartY=4.6 StartZ=0 EndX=3.45 EndY=4.6 EndZ=0
    g34: GeomPoint [constr] X=0 Y=4.6 Z=0
    g35: LineSegment [constr] StartX=-4.93964 StartY=5.1 StartZ=0 EndX=4.93964 EndY=5.1 EndZ=0
    g36: ArcOfCircle [constr] CenterX=0 CenterY=0 CenterZ=0 NormalX=0 NormalY=0 NormalZ=1 AngleXU=0 Radius=7.1 StartAngle=2.34022 EndAngle=7.08456
    g37: GeomPoint [constr] X=0 Y=-7.1 Z=0
    g38: ArcOfCircle [constr] CenterX=0 CenterY=0 CenterZ=0 NormalX=0 NormalY=0 NormalZ=1 AngleXU=0 Radius=7 StartAngle=2.32536 EndAngle=7.09942
    g39: LineSegment [constr] StartX=-4.89898 StartY=5 StartZ=0 EndX=4.89898 EndY=5 EndZ=0
    g40: GeomPoint [constr] X=0 Y=-7 Z=0
  constraints (112):
    c: Coincident(g0,g-1)
    c: Diameter(g0) = 13.2
    c: PointOnObject(g1,g0)
    c: Diameter(g1) = 1
    c: Horizontal(g2)
    c: DistanceY(g0,g2) = 4.6
    c: Coincident(g0,g2)
    c: Coincident(g0,g2)
    c: DistanceY(g1,g0) = 1.2
    c: PointOnObject(g4,g0)
    c: PointOnObject(g5,g0)
    c: PointOnObject(g6,g0)
    c: PointOnObject(g7,g0)
    c: PointOnObject(g3,g0)
    c: PointOnObject(g9,g0)
    c: Equal(g1,g3)
    c: Equal(g3,g4)
    c: Equal(g4,g9)
    c: Equal(g9,g5)
    c: Equal(g5,g6)
    c: Equal(g6,g7)
    c: Equal(g7,g11)
    c: Equal(g11,g12)
    c: Equal(g12,g13)
    c: Equal(g13,g10)
    c: Equal(g10,g8)
    c: PointOnObject(g11,g0)
    c: PointOnObject(g12,g0)
    c: PointOnObject(g13,g0)
    c: PointOnObject(g14,g0)
    c: Coincident(g15,g1)
    c: Coincident(g16,g15)
    c: Coincident(g16,g4)
    c: Coincident(g17,g16)
    c: Coincident(g18,g17)
    c: Coincident(g18,g5)
    c: Coincident(g19,g18)
    c: Coincident(g20,g19)
    c: Coincident(g20,g7)
    c: Coincident(g21,g20)
    c: Coincident(g22,g21)
    c: Coincident(g22,g11)
    c: Coincident(g23,g22)
    c: Coincident(g24,g23)
    c: Coincident(g24,g14)
    c: Coincident(g25,g24)
    c: Coincident(g25,g10)
    c: Coincident(g26,g25)
    c: Coincident(g26,g8)
    c: Coincident(g15,g3)
    c: Coincident(g17,g9)
    c: Coincident(g19,g6)
    c: Coincident(g21,g13)
    c: Coincident(g23,g12)
    c: PointOnObject(g25,g0)
    c: PointOnObject(g26,g0)
    c: Equal(g15,g16)
    c: Equal(g16,g17)
    c: Equal(g17,g18)
    c: Equal(g18,g19)
    c: Equal(g19,g20)
    c: Equal(g20,g21)
    c: Equal(g21,g22)
    c: Equal(g22,g23)
    c: Equal(g23,g24)
    c: Equal(g24,g25)
    c: Equal(g25,g26)
    c: Horizontal(g8,g1)
    c: Equal(g14,g1)
    c: PointOnObject(g27,g2)
    c: Equal(g27,g1)
    c: Coincident(g27,g29)
    c: Coincident(g28,g29)
    c: Distance(g29) = 2.3
    c: Coincident(g28,g31)
    c: Coincident(g30,g31)
    c: Equal(g29,g31)
    c: Parallel(g31,g29)
    c: Coincident(g30,g33)
    c: Coincident(g32,g33)
    c: Equal(g29,g33)
    c: Parallel(g33,g29)
    c: PointOnObject(g34,g-2)
    c: Symmetric(g28,g30,g34)
    c: Equal(g27,g28)
    c: Equal(g28,g30)
    c: Equal(g30,g32)
    c: Horizontal(g33)
    c: Horizontal(g35)
    c: Coincident(g36,g0)
    c: Tangent(g36,g7)
    c: Coincident(g35,g36)
    c: Coincident(g35,g36)
    c: Tangent(g35,g30)
    c: DistanceY(g0,g35) = 5.1
    c: Diameter(g36) = 14.2
    c: PointOnObject(g37,g36)
    c: PointOnObject(g37,g-2)
    c: DistanceY(g37,g35) = 12.2
    c: PointOnObject(g38,g-1)
    c: Diameter(g38) = 14
    c: PointOnObject(g39,g38)
    c: PointOnObject(g39,g38)
    c: Horizontal(g39)
    c: PointOnObject(g38,g-2)
    c: DistanceY(g38,g39) = 5
    c: PointOnObject(g38,g35)
    c: PointOnObject(g38,g35)
    c: DistanceY(g39,g38) = 0.1
    c: PointOnObject(g40,g38)
    c: PointOnObject(g40,g-2)
    c: DistanceY(g37,g40) = 0.1
FEATURE [PartDesign::Pad] Pad002
  BaseFeature = -> Pad
  Direction = (0,0,1)
  Length = 9.5
  Length2 = 10
  Midplane = true
  Profile = -> Sketch002
  ReferenceAxis = -> Sketch002 [N_Axis]
  Refine = true
  Suppressed = false
  Type = 0
FEATURE [Sketcher::SketchObject] Sketch003
  ArcFitTolerance = 0
  AttachmentSupport = -> [XY_Plane]
  FullyConstrained = true
  MakeInternals = false
  MapMode = 5
  sketch-geometry (26):
    g0: ArcOfCircle [constr] CenterX=0 CenterY=0 CenterZ=0 NormalX=0 NormalY=0 NormalZ=1 AngleXU=0 Radius=3.4 StartAngle=2.54863 EndAngle=6.87615
    g1: LineSegment [constr] StartX=-2.81957 StartY=1.9 StartZ=0 EndX=2.81957 EndY=1.9 EndZ=0
    g2: Circle CenterX=-2 CenterY=1.9 CenterZ=0 NormalX=0 NormalY=0 NormalZ=1 AngleXU=0 Radius=0.5
    g3: Circle CenterX=0 CenterY=1.9 CenterZ=0 NormalX=0 NormalY=0 NormalZ=1 AngleXU=0 Radius=0.5
    g4: LineSegment [constr] StartX=-2 StartY=1.9 StartZ=0 EndX=0 EndY=1.9 EndZ=0
    g5: Circle CenterX=2 CenterY=1.9 CenterZ=0 NormalX=0 NormalY=0 NormalZ=1 AngleXU=0 Radius=0.5
    g6: LineSegment [constr] StartX=0 StartY=1.9 StartZ=0 EndX=2 EndY=1.9 EndZ=0
    g7: Circle CenterX=-3.24962 CenterY=1 CenterZ=0 NormalX=0 NormalY=0 NormalZ=1 AngleXU=0 Radius=0.5
    g8: Circle CenterX=-3.22247 CenterY=-1.08429 CenterZ=0 NormalX=0 NormalY=0 NormalZ=1 AngleXU=0 Radius=0.5
    g9: Circle CenterX=-1.98411 CenterY=-2.76103 CenterZ=0 NormalX=0 NormalY=0 NormalZ=1 AngleXU=0 Radius=0.5
    g10: Circle CenterX=0 CenterY=-3.4 CenterZ=0 NormalX=0 NormalY=0 NormalZ=1 AngleXU=0 Radius=0.5
    g11: Circle CenterX=1.98411 CenterY=-2.76103 CenterZ=0 NormalX=0 NormalY=0 NormalZ=1 AngleXU=0 Radius=0.5
    g12: Circle CenterX=3.22247 CenterY=-1.08429 CenterZ=0 NormalX=0 NormalY=0 NormalZ=1 AngleXU=0 Radius=0.5
    g13: Circle CenterX=3.24962 CenterY=1 CenterZ=0 NormalX=0 NormalY=0 NormalZ=1 AngleXU=0 Radius=0.5
    g14: LineSegment [constr] StartX=-3.24962 StartY=1 StartZ=0 EndX=-3.22247 EndY=-1.08429 EndZ=0
    g15: LineSegment [constr] StartX=-3.22247 StartY=-1.08429 StartZ=0 EndX=-1.98411 EndY=-2.76103 EndZ=0
    g16: LineSegment [constr] StartX=-1.98411 StartY=-2.76103 StartZ=0 EndX=0 EndY=-3.4 EndZ=0
    g17: LineSegment [constr] StartX=0 StartY=-3.4 StartZ=0 EndX=1.98411 EndY=-2.76103 EndZ=0
    g18: LineSegment [constr] StartX=1.98411 StartY=-2.76103 StartZ=0 EndX=3.22247 EndY=-1.08429 EndZ=0
    g19: LineSegment [constr] StartX=3.22247 StartY=-1.08429 StartZ=0 EndX=3.24962 EndY=1 EndZ=0
    g20: LineSegment [constr] StartX=-2.53969 StartY=1.4 StartZ=0 EndX=2.53969 EndY=1.4 EndZ=0
    g21: ArcOfCircle [constr] CenterX=0 CenterY=0 CenterZ=0 NormalX=0 NormalY=0 NormalZ=1 AngleXU=0 Radius=2.9 StartAngle=2.63779 EndAngle=6.78699
    g22: ArcOfCircle [constr] CenterX=0 CenterY=0 CenterZ=0 NormalX=0 NormalY=0 NormalZ=1 AngleXU=0 Radius=3 StartAngle=2.61799 EndAngle=6.80678
    g23: LineSegment [constr] StartX=-2.59808 StartY=1.5 StartZ=0 EndX=2.59808 EndY=1.5 EndZ=0
    g24: GeomPoint [constr] X=0 Y=-3 Z=0
    g25: GeomPoint [constr] X=0 Y=-2.9 Z=0
  constraints (73):
    c: Coincident(g0,g-1)
    c: Diameter(g0) = 6.8
    c: Horizontal(g1)
    c: DistanceY(g0,g1) = 1.9
    c: Coincident(g0,g1)
    c: Coincident(g0,g1)
    c: PointOnObject(g2,g1)
    c: Diameter(g2) = 1
    c: Equal(g2,g3) = 1
    c: Coincident(g2,g4)
    c: Coincident(g3,g4)
    c: Distance(g4) = 2
    c: Angle(g4) = 0
    c: Equal(g2,g5) = 1
    c: Coincident(g3,g6)
    c: Coincident(g5,g6)
    c: Equal(g4,g6)
    c: Parallel(g6,g4)
    c: PointOnObject(g3,g-2)
    c: PointOnObject(g7,g0)
    c: PointOnObject(g8,g0)
    c: Equal(g2,g7)
    c: Equal(g7,g8)
    c: Equal(g8,g9)
    c: Equal(g9,g10)
    c: Equal(g10,g11)
    c: Equal(g11,g12)
    c: Equal(g12,g13)
    c: PointOnObject(g9,g0)
    c: PointOnObject(g10,g0)
    c: PointOnObject(g11,g0)
    c: PointOnObject(g12,g0)
    c: PointOnObject(g13,g0)
    c: Coincident(g14,g7)
    c: Coincident(g14,g8)
    c: Coincident(g15,g8)
    c: Coincident(g15,g9)
    c: Coincident(g16,g9)
    c: Coincident(g16,g10)
    c: Coincident(g17,g10)
    c: Coincident(g17,g11)
    c: Coincident(g18,g11)
    c: Coincident(g18,g12)
    c: Coincident(g19,g12)
    c: Coincident(g19,g13)
    c: Equal(g16,g15)
    c: Equal(g15,g14)
    c: Equal(g14,g17)
    c: Equal(g17,g18)
    c: Equal(g18,g19)
    c: DistanceY(g7,g0) = 0.9
    c: Horizontal(g13,g7)
    c: Horizontal(g20)
    c: Tangent(g20,g3)
    c: Coincident(g21,g20)
    c: Diameter(g21) = 5.8
    c: DistanceY(g0,g20) = 1.4
    c: Coincident(g21,g20)
    c: Tangent(g21,g10)
    c: Coincident(g0,g21)
    c: Coincident(g22,g0)
    c: Diameter(g22) = 6
    c: Horizontal(g23)
    c: PointOnObject(g24,g22)
    c: PointOnObject(g24,g-2)
    c: DistanceY(g24,g23) = 4.5
    c: DistanceY(g22,g23) = 1.5
    c: Coincident(g22,g23)
    c: Coincident(g22,g23)
    c: DistanceY(g20,g22) = 0.1
    c: PointOnObject(g25,g21)
    c: PointOnObject(g25,g-2)
    c: DistanceY(g24,g25) = 0.1
FEATURE [PartDesign::Pad] Pad003
  BaseFeature = -> Pad002
  Direction = (0,0,1)
  Length = 9.5
  Length2 = 10
  Midplane = true
  Profile = -> Sketch003
  ReferenceAxis = -> Sketch003 [N_Axis]
  Refine = true
  Suppressed = false
  Type = 0
FEATURE [PartDesign::Plane] DatumPlane001
  AttachmentOffset = pos=(0,0,-4.75) rot=(0,0,1;0rad)
  AttachmentSupport = -> [XY_Plane]
  Length = 60
  MapMode = 5
  Placement = pos=(0,0,-4.75) rot=(0,0,1;0rad)
  ResizeMode = 0
  Width = 60
FEATURE [PartDesign::Plane] DatumPlane
  AttachmentOffset = pos=(0,0,-1.55) rot=(0,0,1;0rad)
  AttachmentSupport = -> [XY_Plane001]
  Length = 60
  MapMode = 5
  Placement = pos=(0,0,-1.55) rot=(0,0,1;0rad)
  ResizeMode = 0
  Width = 60
FEATURE [Sketcher::SketchObject] Sketch006
  ArcFitTolerance = 0
  AttachmentSupport = -> [DatumPlane]
  FullyConstrained = true
  MakeInternals = false
  MapMode = 5
  Placement = pos=(0,0,-1.55) rot=(0,0,1;0rad)
  sketch-geometry (2):
    g0: ArcOfCircle CenterX=0 CenterY=0 CenterZ=0 NormalX=0 NormalY=0 NormalZ=1 AngleXU=0 Radius=3.9 StartAngle=2.47872 EndAngle=6.94606
    g1: LineSegment StartX=-3.07409 StartY=2.4 StartZ=0 EndX=3.07409 EndY=2.4 EndZ=0
  constraints (6):
    c: Coincident(g0,g-1)
    c: Horizontal(g1)
    c: Diameter(g0) = 7.8
    c: DistanceY(g-1,g1) = 2.4
    c: Coincident(g0,g1)
    c: Coincident(g0,g1)
FEATURE [PartDesign::Pad] Pad004
  Direction = (0,0,1)
  Length = 10
  Length2 = 10
  Placement = pos=(0,0,-1.55) rot=(0,0,1;0rad)
  Profile = -> Sketch006
  ReferenceAxis = -> Sketch006 [N_Axis]
  Reversed = true
  Suppressed = false
  Type = 0
FEATURE [Sketcher::SketchObject] Sketch007
  ArcFitTolerance = 0
  AttachmentSupport = -> [YZ_Plane001]
  FullyConstrained = true
  MakeInternals = false
  MapMode = 5
  Placement = pos=(0,0,0) rot=(0.57735,0.57735,0.57735;2.0944rad)
  sketch-geometry (5):
    g0: LineSegment StartX=-1 StartY=-8 StartZ=0 EndX=-1 EndY=8 EndZ=0
    g1: LineSegment StartX=-1 StartY=8 StartZ=0 EndX=1 EndY=8 EndZ=0
    g2: LineSegment StartX=1 StartY=8 StartZ=0 EndX=1 EndY=-8 EndZ=0
    g3: LineSegment StartX=1 StartY=-8 StartZ=0 EndX=-1 EndY=-8 EndZ=0
    g4: GeomPoint [constr] X=0 Y=0 Z=0
  constraints (12):
    c: Coincident(g0,g1)
    c: Coincident(g1,g2)
    c: Coincident(g2,g3)
    c: Coincident(g3,g0)
    c: Horizontal(g1)
    c: Horizontal(g3)
    c: Vertical(g0)
    c: Vertical(g2)
    c: Symmetric(g1,g0,g4)
    c: Coincident(g4,g-1)
    c: DistanceY(g2,g2) = 16
    c: DistanceX(g1,g1) = 2
FEATURE [PartDesign::Pad] Pad005
  BaseFeature = -> Pad004
  Direction = (1,0,0)
  Length = 2
  Length2 = 10
  Midplane = true
  Placement = pos=(0,0,-1.55) rot=(0,0,1;0rad)
  Profile = -> Sketch007
  ReferenceAxis = -> Sketch007 [N_Axis]
  Suppressed = false
  Type = 0
FEATURE [PartDesign::Plane] DatumPlane002
  AttachmentOffset = pos=(0,0,2.25) rot=(0,0,1;0rad)
  AttachmentSupport = -> [XY_Plane002]
  Length = 60
  MapMode = 5
  Placement = pos=(0,0,2.25) rot=(0,0,1;0rad)
  ResizeMode = 0
  Width = 60
FEATURE [Sketcher::SketchObject] Sketch008
  ArcFitTolerance = 0
  AttachmentSupport = -> [DatumPlane002]
  FullyConstrained = true
  MakeInternals = false
  MapMode = 5
  Placement = pos=(0,0,2.25) rot=(0,0,1;0rad)
  sketch-geometry (3):
    g0: ArcOfCircle CenterX=0 CenterY=0 CenterZ=0 NormalX=0 NormalY=0 NormalZ=1 AngleXU=0 Radius=6.1 StartAngle=2.40451 EndAngle=7.02027
    g1: LineSegment StartX=-4.51664 StartY=4.1 StartZ=0 EndX=4.51664 EndY=4.1 EndZ=0
    g2: Circle CenterX=0 CenterY=0 CenterZ=0 NormalX=0 NormalY=0 NormalZ=1 AngleXU=0 Radius=10
  constraints (8):
    c: Coincident(g0,g-1)
    c: Horizontal(g1)
    c: Diameter(g0) = 12.2
    c: DistanceY(g-1,g1) = 4.1
    c: Coincident(g0,g1)
    c: Coincident(g0,g1)
    c: Coincident(g0,g2)
    c: Diameter(g2) = 20
FEATURE [PartDesign::Pad] Pad006
  Direction = (0,0,1)
  Length = 10
  Length2 = 10
  Placement = pos=(0,0,2.25) rot=(0,0,1;0rad)
  Profile = -> Sketch008
  ReferenceAxis = -> Sketch008 [N_Axis]
  Suppressed = false
  Type = 0
FEATURE [Sketcher::SketchObject] Sketch009
  ArcFitTolerance = 0
  AttachmentSupport = -> [YZ_Plane002]
  FullyConstrained = true
  MakeInternals = false
  MapMode = 5
  Placement = pos=(0,0,0) rot=(0.57735,0.57735,0.57735;2.0944rad)
  sketch-geometry (5):
    g0: LineSegment StartX=6 StartY=-5 StartZ=0 EndX=6 EndY=5 EndZ=0
    g1: LineSegment StartX=6 StartY=5 StartZ=0 EndX=8 EndY=5 EndZ=0
    g2: LineSegment StartX=8 StartY=5 StartZ=0 EndX=8 EndY=-5 EndZ=0
    g3: LineSegment StartX=8 StartY=-5 StartZ=0 EndX=6 EndY=-5 EndZ=0
    g4: GeomPoint [constr] X=7 Y=0 Z=0
  constraints (13):
    c: Coincident(g0,g1)
    c: Coincident(g1,g2)
    c: Coincident(g2,g3)
    c: Coincident(g3,g0)
    c: Horizontal(g1)
    c: Horizontal(g3)
    c: Vertical(g0)
    c: Vertical(g2)
    c: Symmetric(g1,g0,g4)
    c: PointOnObject(g4,g-1)
    c: DistanceY(g2,g2) = 10
    c: DistanceX(g1,g1) = 2
    c: DistanceX(g-1,g0) = 6
FEATURE [PartDesign::Pad] Pad007
  BaseFeature = -> Pad006
  Direction = (1,0,0)
  Length = 2
  Length2 = 10
  Midplane = true
  Placement = pos=(0,0,2.25) rot=(0,0,1;0rad)
  Profile = -> Sketch009
  ReferenceAxis = -> Sketch009 [N_Axis]
  Suppressed = false
  Type = 0
FEATURE [Sketcher::SketchObject] Sketch010
  ArcFitTolerance = 0
  AttachmentSupport = -> [DatumPlane001]
  FullyConstrained = true
  MakeInternals = false
  MapMode = 5
  Placement = pos=(0,0,-4.75) rot=(0,0,1;0rad)
  sketch-geometry (4):
    g0: ArcOfCircle CenterX=0 CenterY=0 CenterZ=0 NormalX=0 NormalY=0 NormalZ=1 AngleXU=0 Radius=5 StartAngle=2.49809 EndAngle=6.92669
    g1: LineSegment StartX=-4 StartY=3 StartZ=0 EndX=-4 EndY=5.5 EndZ=0
    g2: LineSegment StartX=-4 StartY=5.5 StartZ=0 EndX=4 EndY=5.5 EndZ=0
    g3: LineSegment StartX=4 StartY=5.5 StartZ=0 EndX=4 EndY=3 EndZ=0
  constraints (11):
    c: Coincident(g0,g-1)
    c: Diameter(g0) = 10
    c: Coincident(g2,g1)
    c: Coincident(g3,g2)
    c: Vertical(g3)
    c: Vertical(g1)
    c: Symmetric(g1,g2,g-2)
    c: DistanceX(g2,g2) = 8
    c: DistanceY(g3,g3) = 2.5
    c: Coincident(g0,g3)
    c: Coincident(g0,g1)
FEATURE [PartDesign::Pocket] Pocket
  BaseFeature = -> Pad003
  Direction = (0,0,-1)
  Length = 2.2
  Length2 = 5
  Profile = -> Sketch010
  ReferenceAxis = -> Sketch010 [N_Axis]
  Reversed = true
  Suppressed = false
  Type = 0
FEATURE [PartDesign::Plane] DatumPlane003
  AttachmentOffset = pos=(0,0,3.75) rot=(0,0,1;0rad)
  AttachmentSupport = -> [XY_Plane001]
  Length = 60
  MapMode = 5
  Placement = pos=(0,0,3.75) rot=(0,0,1;0rad)
  ResizeMode = 0
  Width = 60
FEATURE [Sketcher::SketchObject] Sketch011
  ArcFitTolerance = 0
  AttachmentSupport = -> [DatumPlane003]
  FullyConstrained = true
  MakeInternals = false
  MapMode = 5
  Placement = pos=(0,0,3.75) rot=(0,0,1;0rad)
  sketch-geometry (2):
    g0: ArcOfCircle CenterX=0 CenterY=0 CenterZ=0 NormalX=0 NormalY=0 NormalZ=1 AngleXU=0 Radius=3.88 StartAngle=2.48123 EndAngle=6.94355
    g1: LineSegment StartX=-3.06431 StartY=2.38 StartZ=0 EndX=3.06431 EndY=2.38 EndZ=0
  constraints (6):
    c: Coincident(g0,g-1)
    c: Horizontal(g1)
    c: Coincident(g0,g1)
    c: Coincident(g0,g1)
    c: Diameter(g0) = 7.76
    c: DistanceY(g0,g0) = 2.38
FEATURE [PartDesign::Pad] Pad008
  BaseFeature = -> Pad005
  Direction = (0,0,1)
  Length = 10
  Length2 = 10
  Placement = pos=(0,0,-1.55) rot=(0,0,1;0rad)
  Profile = -> Sketch011
  ReferenceAxis = -> Sketch011 [N_Axis]
  Suppressed = false
  Type = 0
FEATURE [PartDesign::Chamfer] Chamfer
  Angle = 45
  Base = -> Pad008 [Edge19,Edge20,Edge3,Edge5]
  BaseFeature = -> Pad008
  ChamferType = 0
  FlipDirection = false
  Placement = pos=(0,0,-1.55) rot=(0,0,1;0rad)
  Size = 1
  Size2 = 1
  SupportTransform = false
  Suppressed = false
  UseAllEdges = false
FEATURE [PartDesign::Body] Body001
  AllowCompound = false
  Group = -> [DatumPlane,Sketch006,Pad004,Sketch007,Pad005,DatumPlane003,Sketch011,Pad008,Chamfer]
  Origin = -> Origin001
  Tip = -> Chamfer
FEATURE [PartDesign::Boolean] Boolean
  BaseFeature = -> Pocket
  Group = -> [Body001]
  Suppressed = false
  Type = 1
  UsePlacement = false
FEATURE [PartDesign::Plane] DatumPlane004
  AttachmentOffset = pos=(0,0,-3.75) rot=(0,0,1;0rad)
  AttachmentSupport = -> [XY_Plane002]
  Length = 60
  MapMode = 5
  Placement = pos=(0,0,-3.75) rot=(0,0,1;0rad)
  ResizeMode = 0
  Width = 60
FEATURE [Sketcher::SketchObject] Sketch012
  ArcFitTolerance = 0
  AttachmentSupport = -> [DatumPlane004]
  FullyConstrained = true
  MakeInternals = false
  MapMode = 5
  Placement = pos=(0,0,-3.75) rot=(0,0,1;0rad)
  sketch-geometry (3):
    g0: ArcOfCircle CenterX=0 CenterY=0 CenterZ=0 NormalX=0 NormalY=0 NormalZ=1 AngleXU=0 Radius=6.1 StartAngle=2.40451 EndAngle=7.02027
    g1: Circle CenterX=0 CenterY=0 CenterZ=0 NormalX=0 NormalY=0 NormalZ=1 AngleXU=0 Radius=10
    g2: LineSegment StartX=-4.51664 StartY=4.1 StartZ=0 EndX=4.51664 EndY=4.1 EndZ=0
  constraints (8):
    c: Coincident(g0,g-1)
    c: Coincident(g1,g0)
    c: Horizontal(g2)
    c: DistanceY(g0,g2) = 4.1
    c: Diameter(g0) = 12.2
    c: Diameter(g1) = 20
    c: Coincident(g0,g2)
    c: Coincident(g0,g2)
FEATURE [PartDesign::Pad] Pad009
  BaseFeature = -> Pad007
  Direction = (0,0,1)
  Length = 10
  Length2 = 10
  Placement = pos=(0,0,2.25) rot=(0,0,1;0rad)
  Profile = -> Sketch012
  ReferenceAxis = -> Sketch012 [N_Axis]
  Reversed = true
  Suppressed = false
  Type = 0
FEATURE [PartDesign::Chamfer] Chamfer001
  Angle = 45
  Base = -> Pad009 [Edge24,Edge23]
  BaseFeature = -> Pad009
  ChamferType = 0
  FlipDirection = false
  Placement = pos=(0,0,2.25) rot=(0,0,1;0rad)
  Size = 1
  Size2 = 1
  SupportTransform = false
  Suppressed = false
  UseAllEdges = false
FEATURE [PartDesign::Chamfer] Chamfer002
  Angle = 70
  Base = -> Chamfer001 [Edge27,Edge28]
  BaseFeature = -> Chamfer001
  ChamferType = 2
  FlipDirection = false
  Placement = pos=(0,0,2.25) rot=(0,0,1;0rad)
  Size = 1
  Size2 = 3
  SupportTransform = false
  Suppressed = false
  UseAllEdges = false
FEATURE [PartDesign::Body] Body002
  AllowCompound = false
  Group = -> [DatumPlane002,Sketch008,Pad006,Sketch009,Pad007,DatumPlane004,Sketch012,Pad009,Chamfer001,Chamfer002]
  Origin = -> Origin002
  Tip = -> Chamfer002
FEATURE [PartDesign::Boolean] Boolean001
  BaseFeature = -> Boolean
  Group = -> [Body002]
  Suppressed = false
  Type = 1
  UsePlacement = false
FEATURE [PartDesign::CoordinateSystem] LCS_1
  AttacherType = Attacher::AttachEngine3D
  AttachmentOffset = pos=(0,0,0) rot=(0,0,-1;2.47837rad)
  AttachmentSupport = -> [Boolean001]
  MapMode = 11
  Placement = pos=(-4e-16,0,4.75) rot=(0,0,1;1.57366rad)
FEATURE [PartDesign::CoordinateSystem] LCS_2
  AttacherType = Attacher::AttachEngine3D
  AttachmentOffset = pos=(0,0,0) rot=(0,0,-1;2.47837rad)
  AttachmentSupport = -> [Boolean001]
  MapMode = 11
  Placement = pos=(-4e-16,0,-2.55) rot=(0,0,1;1.57115rad)
FEATURE [PartDesign::CoordinateSystem] LCS_3
  AttacherType = Attacher::AttachEngine3D
  AttachmentSupport = -> [Boolean001]
  MapMode = 5
  Placement = pos=(0,0,-4.75) rot=(1,0,0;3.14159rad)
FEATURE [PartDesign::Body] Body  label="PLASTIC-TEK2-KNOB-INTERFACE"
  AllowCompound = false
  Group = -> [Sketch,Pad,Pad002,Sketch002,Sketch003,Pad003,DatumPlane001,Pocket,Sketch010,Boolean,Boolean001,LCS_1,LCS_2,LCS_3]
  Origin = -> Origin
  Tip = -> Boolean001
---- part KNOB-TEK2_assembly_tool.FCStd = doc fcstd_d594af51a4cf ----
FCSTD DOCUMENT  (FreeCAD 1.0R39319 (Git))
Label: KNOB-TEK2_assembly_tool
License: All rights reserved
LicenseURL: https://en.wikipedia.org/wiki/All_rights_reserved
objects: Sketcher::SketchObject×3, PartDesign::CoordinateSystem×1, PartDesign::Revolution×1, PartDesign::Chamfer×1, PartDesign::Body×1
note: 14 computed .brp shape members not serialized (recipe doc carries the construction recipe); baked Part::Feature solids carry a one-line shape summary decoded from their .brp

FEATURE [Sketcher::SketchObject] Sketch
  ArcFitTolerance = 0
  AttachmentSupport = -> [XY_Plane]
  FullyConstrained = true
  MakeInternals = false
  MapMode = 5
  sketch-geometry (2):
    g0: ArcOfCircle CenterX=0 CenterY=0 CenterZ=0 NormalX=0 NormalY=0 NormalZ=1 AngleXU=0 Radius=2.7 StartAngle=2.87934 EndAngle=6.54544
    g1: LineSegment StartX=-2.60768 StartY=0.7 StartZ=0 EndX=2.60768 EndY=0.7 EndZ=0
  constraints (6):
    c: Coincident(g0,g-1)
    c: Diameter(g0) = 5.4
    c: Horizontal(g1)
    c: DistanceY(g0,g1) = 0.7
    c: Coincident(g0,g1)
    c: Coincident(g0,g1)
FEATURE [Sketcher::SketchObject] Sketch001
  ArcFitTolerance = 0
  AttachmentSupport = -> [XY_Plane]
  FullyConstrained = true
  MakeInternals = false
  MapMode = 5
  sketch-geometry (1):
    g0: Circle CenterX=0 CenterY=0 CenterZ=0 NormalX=0 NormalY=0 NormalZ=1 AngleXU=0 Radius=7.5
  constraints (2):
    c: Coincident(g0,g-1)
    c: Diameter(g0) = 15
FEATURE [PartDesign::CoordinateSystem] LCS_1
  AttacherType = Attacher::AttachEngine3D
  MapMode = 5
  Placement = pos=(0,0,0) rot=(1,0,0;3.14159rad)
FEATURE [Sketcher::SketchObject] Sketch_1
  ArcFitTolerance = 1e-06
  AttachmentSupport = -> [YZ_Plane]
  FullyConstrained = true
  MakeInternals = false
  MapMode = 5
  Placement = pos=(0,0,0) rot=(0.57735,0.57735,0.57735;2.0944rad)
  sketch-geometry (8):
    g0: LineSegment StartX=0 StartY=0 StartZ=0 EndX=-7.5 EndY=0 EndZ=0
    g1: LineSegment StartX=-7.5 StartY=0 StartZ=0 EndX=-7.5 EndY=4.5 EndZ=0
    g2: LineSegment StartX=-7.5 StartY=4.5 StartZ=0 EndX=-15 EndY=4.5 EndZ=0
    g3: LineSegment StartX=-15 StartY=4.5 StartZ=0 EndX=-15 EndY=9.5 EndZ=0
    g4: LineSegment StartX=-15 StartY=9.5 StartZ=0 EndX=-10 EndY=9.5 EndZ=0
    g5: LineSegment StartX=-10 StartY=9.5 StartZ=0 EndX=-10 EndY=12.5 EndZ=0
    g6: LineSegment StartX=-10 StartY=12.5 StartZ=0 EndX=0 EndY=12.5 EndZ=0
    g7: LineSegment StartX=0 StartY=12.5 StartZ=0 EndX=0 EndY=0 EndZ=0
  constraints (23):
    c: Coincident(g0,g-1)
    c: PointOnObject(g0,g-1)
    c: Coincident(g1,g0)
    c: Vertical(g1)
    c: Coincident(g2,g1)
    c: Horizontal(g2)
    c: Coincident(g3,g2)
    c: Vertical(g3)
    c: Coincident(g4,g3)
    c: Horizontal(g4)
    c: Coincident(g5,g4)
    c: Coincident(g6,g5)
    c: PointOnObject(g6,g-2)
    c: Horizontal(g6)
    c: Coincident(g7,g6)
    c: Coincident(g7,g0)
    c: Vertical(g5)
    c: DistanceY(g1,g1) = 4.5
    c: DistanceY(g3,g3) = 5
    c: DistanceY(g5,g5) = 3
    c: Distance(g7,g1) = 7.5
    c: Distance(g-2,g3) = 15
    c: DistanceX(g6,g6) = 10
FEATURE [PartDesign::Revolution] Revolution
  Angle = 360
  Angle2 = 60
  Axis = (0,0,1)
  Base = (0,0,0)
  Placement = pos=(0,0,0) rot=(1,1,1;2.0944rad)
  Profile = -> Sketch_1
  ReferenceAxis = -> Sketch_1 [V_Axis]
  Refine = true
  Suppressed = false
  Type = 0
FEATURE [PartDesign::Chamfer] Chamfer
  Angle = 45
  Base = -> Revolution [Edge1,Edge8]
  BaseFeature = -> Revolution
  ChamferType = 0
  FlipDirection = false
  Placement = pos=(0,0,0) rot=(1,1,1;2.0944rad)
  Refine = true
  Size = 1
  Size2 = 1
  SupportTransform = false
  Suppressed = false
  UseAllEdges = false
FEATURE [PartDesign::Body] Body
  AllowCompound = false
  Group = -> [Sketch,Sketch001,LCS_1,Sketch_1,Revolution,Chamfer]
  Origin = -> Origin
  Tip = -> Chamfer
